# Revit family: 02_HSDUO80-52_D
name_source: partatom
category: Porte
units: mm (PartAtom-declared; Revit-internal decimal feet)

## family parameters
Condiviso = No
Host = Muro
Numero OmniClass = 23.30.10.00
Punto di calcolo locali = Sì
Sempre verticale = Sì
Taglio con vuoti quando caricato = No
Titolo OmniClass = Doors

## types (2) — shared parameters
Altezza = 2100 mm
Chiusura muro = Per host
Codice assieme = B2030100
Costruzione analitica = <Nessuno>
D1 = 1000 mm  [stored 3.28084 ft]
D2 = 1000 mm  [stored 3.28084 ft]
DIM1_anta scorrevole = 1000 mm  [stored 3.28084 ft]
DIM2_anta scorrevole = 1000 mm  [stored 3.28084 ft]
EXTERNAL ALUMINUM FRAME/TELAIO ALLUMINIO ESTERNO = UNIFORM_ALUMINUM
Funzione = Interno
GLASS WEIGHT/PESO VETRO = 43.00 kg/m²
H = 2100 mm
HANDLE HEIGHT/ALTEZZA MANIGLIA = 1100 mm
HANDLE/MANIGLIA = UNIFORM_ALUMINUM
HOLE_H = 2100 mm
HOLE_W = 2028 mm  [stored 6.65354 ft]
INTERIOR WOOD FRAME/TELAIO LEGNO INTERNO = UNIFORM_WOOD
Immagine tipo = <Nessuno>
Larghezza = 2000 mm  [stored 6.56168 ft]
Larghezza telaio = 75 mm
MAXIMUM HEIGHT/ALTEZZA MASSIMA = 3200 mm  [stored 10.4987 ft]
MAXIMUM WIDTH/LARGHEZZA MASSIMA = 5500 mm  [stored 18.0446 ft]
MAX_DIMENSIONS_WARNING = No
MINIMUM HEIGHT/ALTEZZA MINIMA = 1200 mm  [stored 3.93701 ft]
MINIMUM WIDTH/LARGHEZZA MINIMA  = 1200 mm  [stored 3.93701 ft]
Modello = DUO
PRODUCER WEBSITE/SITO WEB PRODUTTORE = www.uniform.it
PRODUCT WEBSITE/SITO WEB PRODOTTO = www.sistema-uni-one.it
Produttore = UNIFORM
Proiezione telaio est. = 25 mm  [stored 0.082021 ft]
Proiezione telaio int. = 25 mm  [stored 0.082021 ft]
URL = https://www.sistema-uni-one.it
W = 2028 mm  [stored 6.65354 ft]
WINDOW GLASS/VETRO FINESTRA = UNIFORM_GLASS
zero-valued in all types: T_F_H, WINDOW HOLE TOLERANCE/TOLLERANZA FORO FINESTRA

## per-type parameters (varying)
| type | Ug GLASS/Ug VETRO | Uw WINDOW/Uw FINESTRA |
| DUO_2_SLIDE_AS_THERMAL | 1.0000 W/(m²·K) | 1.2000 W/(m²·K) |
| DUO_2_SLIDE_AS_HIGH THERMAL PERFORMANCE | 0.5000 W/(m²·K) | 0.8000 W/(m²·K) |

note: [stored X ft] marks values corroborated as IEEE doubles in the binary element streams (Revit-internal decimal feet)
